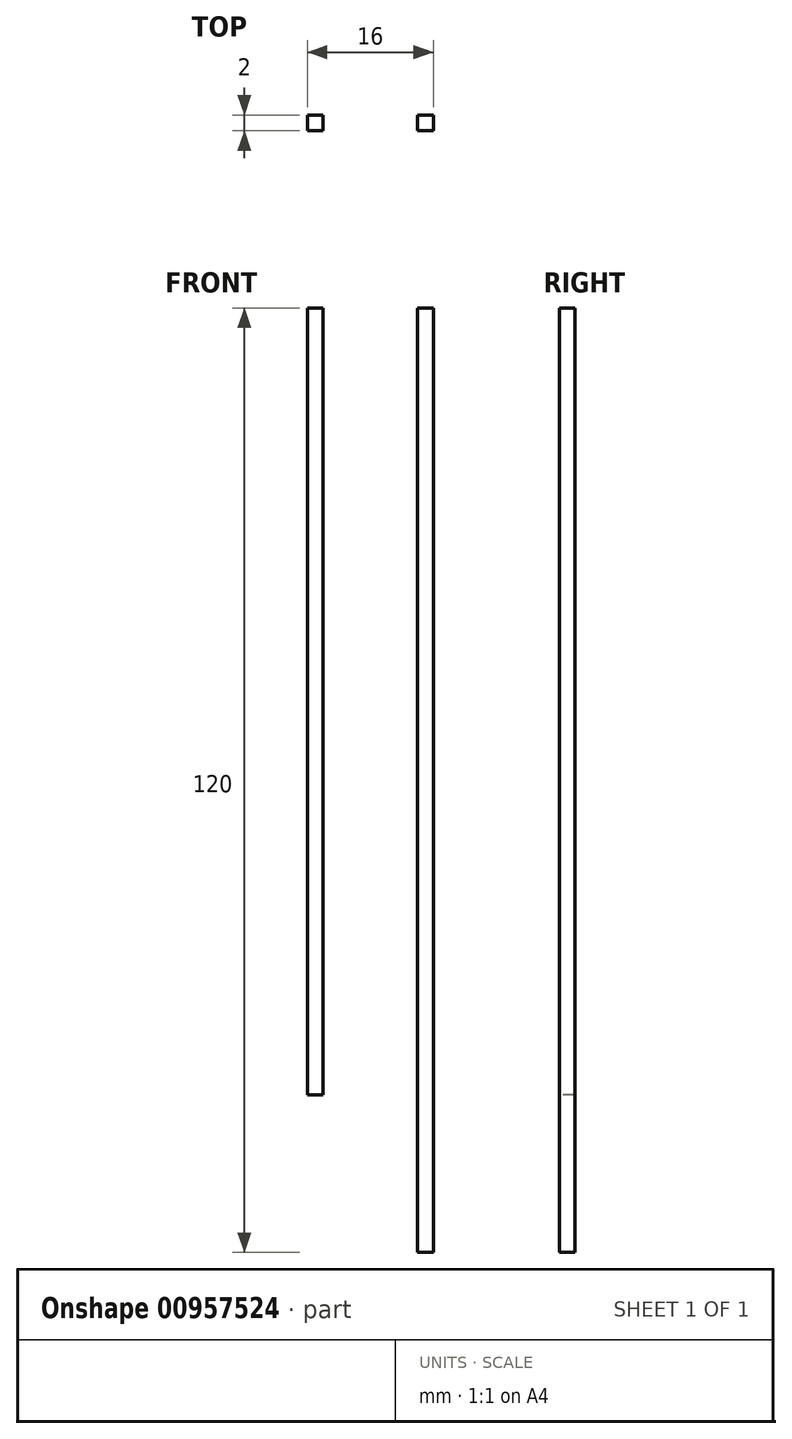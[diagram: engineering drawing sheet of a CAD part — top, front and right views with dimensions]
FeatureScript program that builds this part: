
annotation { "Feature Type Name" : "Feature", "Feature Type Description" : "" }
export const myFeature = defineFeature(function(context is Context, id is Id, definition is map)
    precondition{}
    {
        {
            var Q0;
            Q0=qCreatedBy(makeId("Front.planeOp"),FACE);
            var sketch = newSketch(context, id + "F0", { "sketchPlane" : qUnion([Q0])});
            skLineSegment(sketch, "E0", {"start": v(0, 91.83) * mm, "end": v(0, -102.43) * mm, "construction": true});
            skSolve(sketch);
        }
        {
            var Q0;
            Q0=qCreatedBy(makeId("Front.planeOp"),FACE);
            var sketch = newSketch(context, id + "F1", { "sketchPlane" : qUnion([Q0])});
            skArc(sketch, "E1", {"start": v(10.59, 0) * mm, "mid": v(7.49, 7.49) * mm, "end": v(0, 10.59) * mm});
            skLineSegment(sketch, "E2", {"start": v(10.59, 0) * mm, "end": v(10.59, -19.62) * mm});
            skLineSegment(sketch, "E3", {"start": v(10.59, -19.62) * mm, "end": v(10.59, -19.62) * mm});
            skLineSegment(sketch, "E4", {"start": v(10.59, -19.62) * mm, "end": v(14.23, -19.62) * mm});
            skLineSegment(sketch, "E5", {"start": v(14.23, -19.62) * mm, "end": v(14.23, -22.27) * mm});
            skLineSegment(sketch, "E6", {"start": v(14.23, -22.27) * mm, "end": v(0, -22.27) * mm});
            skSolve(sketch);
        }
        {
            var Q0;
            Q0=sQuery(id+"F1.wireOp",EDGE,"E2");
            var Q1;
            Q1=sQuery(id+"F1.wireOp",EDGE,"E1");
            var Q2;
            Q2=sQuery(id+"F1.wireOp",EDGE,"E4");
            var Q3;
            Q3=sQuery(id+"F1.wireOp",EDGE,"E6");
            var Q4;
            Q4=sQuery(id+"F1.wireOp",EDGE,"E5");
            var Q5;
            Q5=sQuery(id+"F0.wireOp",EDGE,"E0");
            revolve(context, id + "F2", {"bodyType" : ToolBodyType.SURFACE, "operationType" : NewBodyOperationType.ADD, "surfaceOperationType" : NewSurfaceOperationType.NEW, "surfaceEntities" : qUnion([Q0, Q1, Q2, Q3, Q4]), "axis" : qUnion([Q5]), "revolveType" : RevolveType.FULL});
        }
        {
            var Q0;
            Q0=makeQuery(id+"F2.opRevolve","SWEPT_FACE",FACE,{"disambiguationData":[OSD([sQuery(id+"F1.wireOp",EDGE,"E6")])]});
            var sketch = newSketch(context, id + "F3", { "sketchPlane" : qUnion([Q0])});
            skPoint(sketch, "E7", {"position": v(7, 0) * mm});
            skPoint(sketch, "E8", {"position": v(-7, 0) * mm});
            skLineSegment(sketch, "E9.bottom", {"start": v(8, 1) * mm, "end": v(6, 1) * mm});
            skLineSegment(sketch, "E9.top", {"start": v(8, -1) * mm, "end": v(6, -1) * mm});
            skLineSegment(sketch, "E9.left", {"start": v(8, 1) * mm, "end": v(8, -1) * mm});
            skLineSegment(sketch, "E9.right", {"start": v(6, 1) * mm, "end": v(6, -1) * mm});
            skLineSegment(sketch, "E10.bottom", {"start": v(-6, 1) * mm, "end": v(-8, 1) * mm});
            skLineSegment(sketch, "E10.top", {"start": v(-6, -1) * mm, "end": v(-8, -1) * mm});
            skLineSegment(sketch, "E10.left", {"start": v(-6, 1) * mm, "end": v(-6, -1) * mm});
            skLineSegment(sketch, "E10.right", {"start": v(-8, 1) * mm, "end": v(-8, -1) * mm});
            skSolve(sketch);
        }
        {
            var Q0;
            Q0=makeQuery(id+"F3.imprint","IMPRINT",FACE,{"disambiguationData":[TD([[makeQuery(id+"F3.imprint","IMPRINT",EDGE,{"derivedFrom":sQuery(id+"F3.wireOp",EDGE,"E9.bottom")}),1.0]])]});
            extrude(context, id + "F4", {"entities" : qUnion([Q0]), "oppositeDirection" : true, "depth" : 120 * mm, "offsetDistance" : 25 * mm});
        }
        {
            var Q0;
            Q0=makeQuery(id+"F3.imprint","IMPRINT",FACE,{"disambiguationData":[TD([[makeQuery(id+"F3.imprint","IMPRINT",EDGE,{"derivedFrom":sQuery(id+"F3.wireOp",EDGE,"E10.bottom")}),1.0]])]});
            extrude(context, id + "F5", {"entities" : qUnion([Q0]), "oppositeDirection" : true, "depth" : 100 * mm, "offsetDistance" : 25 * mm});
        }
    });
